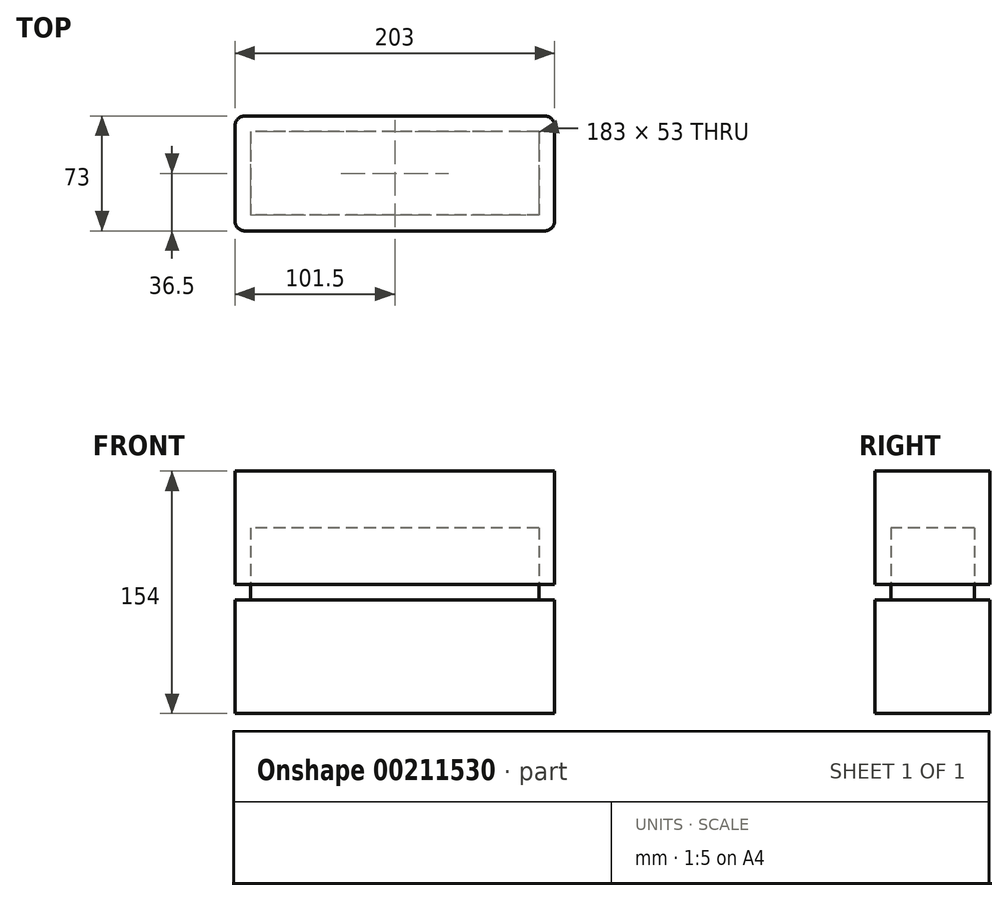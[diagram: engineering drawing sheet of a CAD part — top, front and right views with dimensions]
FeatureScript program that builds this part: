
annotation { "Feature Type Name" : "Feature", "Feature Type Description" : "" }
export const myFeature = defineFeature(function(context is Context, id is Id, definition is map)
    precondition{}
    {
        {
            var Q0;
            Q0=qCreatedBy(makeId("Top.planeOp"),FACE);
            var sketch = newSketch(context, id + "F0", { "sketchPlane" : qUnion([Q0])});
            skLineSegment(sketch, "E0.bottom", {"start": v(101.5, 36.5) * mm, "end": v(-101.5, 36.5) * mm});
            skLineSegment(sketch, "E0.top", {"start": v(101.5, -36.5) * mm, "end": v(-101.5, -36.5) * mm});
            skLineSegment(sketch, "E0.left", {"start": v(101.5, 36.5) * mm, "end": v(101.5, -36.5) * mm});
            skLineSegment(sketch, "E0.right", {"start": v(-101.5, 36.5) * mm, "end": v(-101.5, -36.5) * mm});
            skPoint(sketch, "E0.middle", {"position": v(0, 0) * mm});
            skLineSegment(sketch, "E1.0", {"start": v(-91.5, 26.5) * mm, "end": v(-91.5, -26.5) * mm});
            skLineSegment(sketch, "E1.1", {"start": v(91.5, 26.5) * mm, "end": v(-91.5, 26.5) * mm});
            skLineSegment(sketch, "E1.2", {"start": v(91.5, 26.5) * mm, "end": v(91.5, -26.5) * mm});
            skLineSegment(sketch, "E1.3", {"start": v(91.5, -26.5) * mm, "end": v(-91.5, -26.5) * mm});
            skSolve(sketch);
        }
        {
            var Q0;
            Q0=makeQuery(id+"F0.imprint","IMPRINT",FACE,{"disambiguationData":[TD([[makeQuery(id+"F0.imprint","IMPRINT",EDGE,{"derivedFrom":sQuery(id+"F0.wireOp",EDGE,"E0.bottom")}),1.0]])]});
            var Q1;
            Q1=makeQuery(id+"F0.imprint","IMPRINT",FACE,{"disambiguationData":[TD([[makeQuery(id+"F0.imprint","IMPRINT",EDGE,{"derivedFrom":sQuery(id+"F0.wireOp",EDGE,"E1.0")}),1.0]])]});
            extrude(context, id + "F1", {"entities" : qUnion([Q0, Q1]), "oppositeDirection" : true, "depth" : 72 * mm});
        }
        {
            var Q0;
            Q0=makeQuery(id+"F0.imprint","IMPRINT",FACE,{"disambiguationData":[TD([[makeQuery(id+"F0.imprint","IMPRINT",EDGE,{"derivedFrom":sQuery(id+"F0.wireOp",EDGE,"E1.0")}),1.0]])]});
            extrude(context, id + "F2", {"entities" : qUnion([Q0]), "operationType" : NewBodyOperationType.ADD, "depth" : 36 * mm});
        }
        {
            var Q0;
            Q0=makeQuery(id+"F1.opExtrude","CAP_FACE",FACE,{"disambiguationData":[OSD([sQuery(id+"F0.wireOp",EDGE,"E0.bottom"),sQuery(id+"F0.wireOp",EDGE,"E0.top"),sQuery(id+"F0.wireOp",EDGE,"E0.left"),sQuery(id+"F0.wireOp",EDGE,"E0.right")])],"isStart":true});
            cPlane(context, id + "F3", {"entities" : qUnion([Q0]), "cplaneType" : CPlaneType.OFFSET, "offset" : 10 * mm, "width" : 150 * mm, "height" : 150 * mm});
        }
        {
            var Q0;
            Q0=qCreatedBy(id+"F3.planeOp",FACE);
            var sketch = newSketch(context, id + "F4", { "sketchPlane" : qUnion([Q0])});
            skLineSegment(sketch, "E2.bottom", {"start": v(101.5, 36.5) * mm, "end": v(-101.5, 36.5) * mm});
            skLineSegment(sketch, "E2.top", {"start": v(101.5, -36.5) * mm, "end": v(-101.5, -36.5) * mm});
            skLineSegment(sketch, "E2.left", {"start": v(101.5, 36.5) * mm, "end": v(101.5, -36.5) * mm});
            skLineSegment(sketch, "E2.right", {"start": v(-101.5, 36.5) * mm, "end": v(-101.5, -36.5) * mm});
            skPoint(sketch, "E2.middle", {"position": v(0, 0) * mm});
            skLineSegment(sketch, "E3.0", {"start": v(91.5, 26.5) * mm, "end": v(-91.5, 26.5) * mm});
            skLineSegment(sketch, "E3.1", {"start": v(91.5, 26.5) * mm, "end": v(91.5, -26.5) * mm});
            skLineSegment(sketch, "E3.2", {"start": v(91.5, -26.5) * mm, "end": v(-91.5, -26.5) * mm});
            skLineSegment(sketch, "E3.3", {"start": v(-91.5, 26.5) * mm, "end": v(-91.5, -26.5) * mm});
            skSolve(sketch);
        }
        {
            var Q0;
            Q0=makeQuery(id+"F4.imprint","IMPRINT",FACE,{"disambiguationData":[TD([[makeQuery(id+"F4.imprint","IMPRINT",EDGE,{"derivedFrom":sQuery(id+"F4.wireOp",EDGE,"E2.bottom")}),1.0]])]});
            var Q1;
            Q1=makeQuery(id+"F4.imprint","IMPRINT",FACE,{"disambiguationData":[TD([[makeQuery(id+"F4.imprint","IMPRINT",EDGE,{"derivedFrom":sQuery(id+"F4.wireOp",EDGE,"E3.0")}),1.0]])]});
            extrude(context, id + "F5", {"entities" : qUnion([Q0, Q1]), "depth" : 72 * mm});
        }
        {
            var Q0;
            Q0=makeQuery(id+"F4.imprint","IMPRINT",FACE,{"disambiguationData":[TD([[makeQuery(id+"F4.imprint","IMPRINT",EDGE,{"derivedFrom":sQuery(id+"F4.wireOp",EDGE,"E3.0")}),1.0]])]});
            extrude(context, id + "F6", {"entities" : qUnion([Q0]), "operationType" : NewBodyOperationType.REMOVE, "depth" : 36 * mm});
        }
        {
            var Q0;
            Q0=makeQuery(id+"F5.opExtrude","SWEPT_EDGE",EDGE,{"disambiguationData":[OSD([sQuery(id+"F4.wireOp",EDGE,"E2.bottom"),sQuery(id+"F4.wireOp",EDGE,"E2.left")])]});
            var Q1;
            Q1=makeQuery(id+"F1.opExtrude","SWEPT_EDGE",EDGE,{"disambiguationData":[OSD([sQuery(id+"F0.wireOp",EDGE,"E0.bottom"),sQuery(id+"F0.wireOp",EDGE,"E0.left")])]});
            var Q2;
            Q2=makeQuery(id+"F1.opExtrude","SWEPT_EDGE",EDGE,{"disambiguationData":[OSD([sQuery(id+"F0.wireOp",EDGE,"E0.top"),sQuery(id+"F0.wireOp",EDGE,"E0.left")])]});
            var Q3;
            Q3=makeQuery(id+"F5.opExtrude","SWEPT_EDGE",EDGE,{"disambiguationData":[OSD([sQuery(id+"F4.wireOp",EDGE,"E2.top"),sQuery(id+"F4.wireOp",EDGE,"E2.left")])]});
            var Q4;
            Q4=makeQuery(id+"F5.opExtrude","SWEPT_EDGE",EDGE,{"disambiguationData":[OSD([sQuery(id+"F4.wireOp",EDGE,"E2.bottom"),sQuery(id+"F4.wireOp",EDGE,"E2.right")])]});
            var Q5;
            Q5=makeQuery(id+"F1.opExtrude","SWEPT_EDGE",EDGE,{"disambiguationData":[OSD([sQuery(id+"F0.wireOp",EDGE,"E0.bottom"),sQuery(id+"F0.wireOp",EDGE,"E0.right")])]});
            var Q6;
            Q6=makeQuery(id+"F5.opExtrude","SWEPT_EDGE",EDGE,{"disambiguationData":[OSD([sQuery(id+"F4.wireOp",EDGE,"E2.top"),sQuery(id+"F4.wireOp",EDGE,"E2.right")])]});
            var Q7;
            Q7=makeQuery(id+"F1.opExtrude","SWEPT_EDGE",EDGE,{"disambiguationData":[OSD([sQuery(id+"F0.wireOp",EDGE,"E0.top"),sQuery(id+"F0.wireOp",EDGE,"E0.right")])]});
            fillet(context, id + "F7", {"entities" : qUnion([Q0, Q1, Q2, Q3, Q4, Q5, Q6, Q7]), "radius" : 6.35 * mm, "tangentPropagation" : true, "allowEdgeOverflow" : false});
        }
    });
